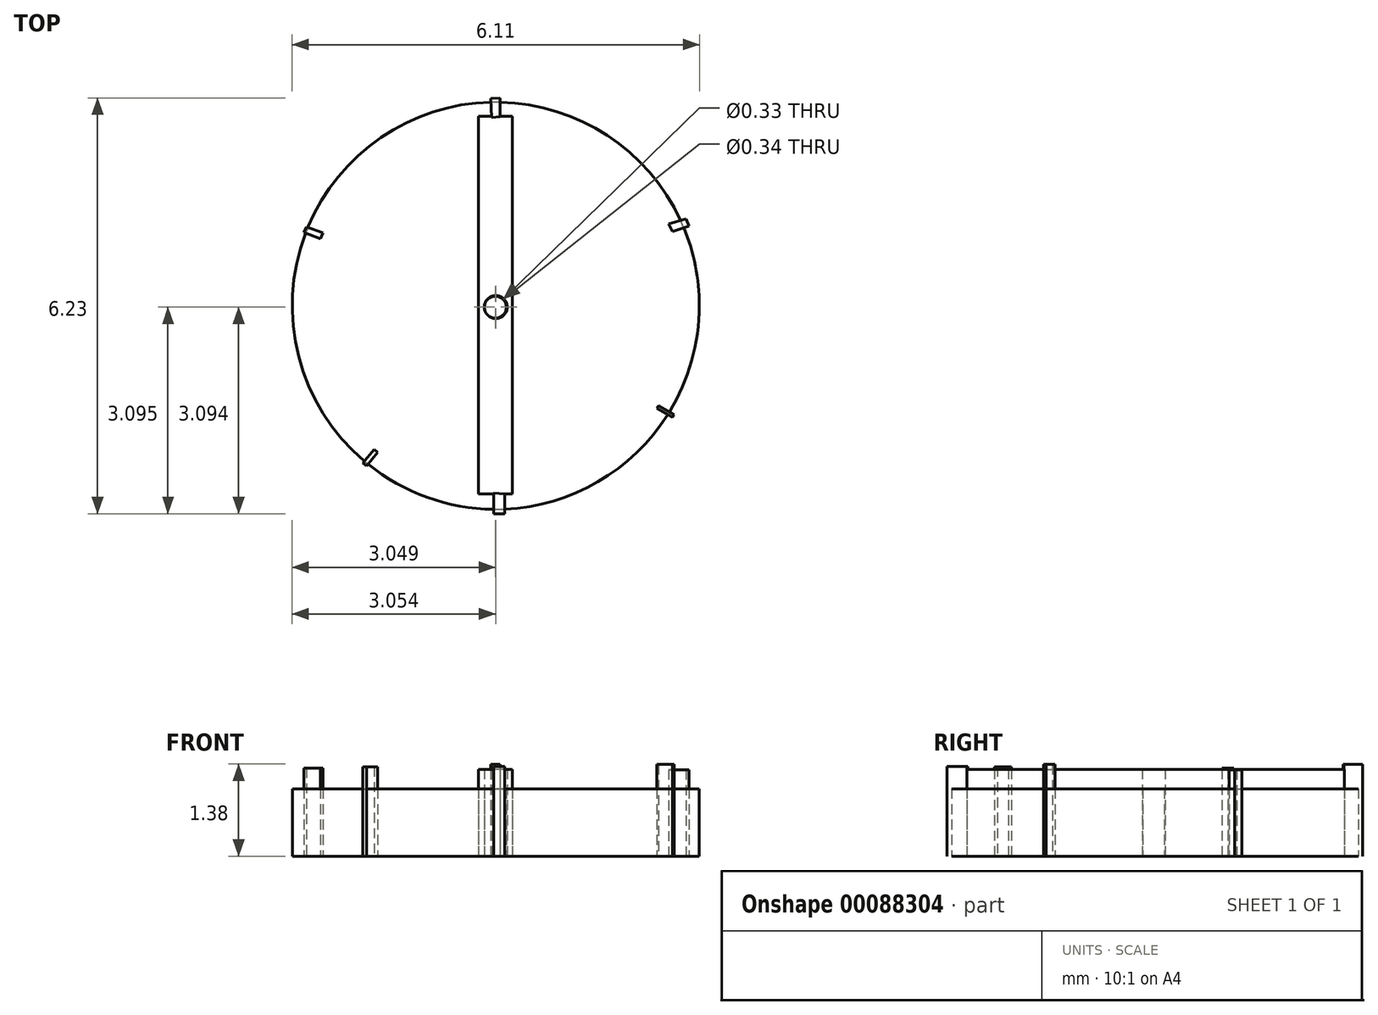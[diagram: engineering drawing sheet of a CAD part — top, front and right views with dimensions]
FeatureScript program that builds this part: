
annotation { "Feature Type Name" : "Feature", "Feature Type Description" : "" }
export const myFeature = defineFeature(function(context is Context, id is Id, definition is map)
    precondition{}
    {
        {
            var Q0;
            Q0=qCreatedBy(makeId("Top.planeOp"),FACE);
            var sketch = newSketch(context, id + "F0", { "sketchPlane" : qUnion([Q0])});
            skLineSegment(sketch, "E0", {"start": v(-40, 21.65) * mm, "end": v(-40, 15.99) * mm});
            skLineSegment(sketch, "E1", {"start": v(-40, 15.99) * mm, "end": v(-39.49, 15.99) * mm});
            skLineSegment(sketch, "E2", {"start": v(-39.49, 15.99) * mm, "end": v(-39.49, 21.65) * mm});
            skLineSegment(sketch, "E3", {"start": v(-39.49, 21.65) * mm, "end": v(-40, 21.65) * mm});
            skCircle(sketch, "E4", {"center": v(-39.77, 18.82) * mm, "radius": 2.9 * mm});
            skPoint(sketch, "E4.centerSnap0", {"position": v(-40, 18.82) * mm});
            skCircle(sketch, "E5", {"center": v(-39.77, 18.82) * mm, "radius": 3.38 * mm});
            skSolve(sketch);
        }
        {
            var Q0;
            Q0=makeQuery(id+"F0.imprint","IMPRINT",FACE,{"disambiguationData":[TD([[makeQuery(id+"F0.imprint","IMPRINT",EDGE,{"derivedFrom":sQuery(id+"F0.wireOp",EDGE,"E0")}),1.0]])]});
            extrude(context, id + "F1", {"entities" : qUnion([Q0]), "depth" : 1.3 * mm});
        }
        {
            var Q0;
            Q0=qCreatedBy(makeId("Top.planeOp"),FACE);
            var sketch = newSketch(context, id + "F2", { "sketchPlane" : qUnion([Q0])});
            skLineSegment(sketch, "E6", {"start": v(-42.36, 19.8) * mm, "end": v(-42.61, 19.9) * mm});
            skLineSegment(sketch, "E7", {"start": v(-42.33, 19.9) * mm, "end": v(-42.58, 19.99) * mm});
            skLineSegment(sketch, "E8", {"start": v(-42.33, 19.9) * mm, "end": v(-42.36, 19.8) * mm});
            skLineSegment(sketch, "E9", {"start": v(-42.58, 19.99) * mm, "end": v(-42.61, 19.9) * mm});
            skSolve(sketch);
        }
        {
            var Q0;
            Q0 = qSketchRegion(id + "F2", true);
            extrude(context, id + "F3", {"entities" : qUnion([Q0]), "depth" : 1.32 * mm});
        }
        {
            var Q0;
            Q0=qCreatedBy(makeId("Top.planeOp"),FACE);
            var sketch = newSketch(context, id + "F4", { "sketchPlane" : qUnion([Q0])});
            skLineSegment(sketch, "E10", {"start": v(-37.09, 19.92) * mm, "end": v(-36.84, 20) * mm});
            skLineSegment(sketch, "E11", {"start": v(-37.14, 20.03) * mm, "end": v(-36.88, 20.11) * mm});
            skLineSegment(sketch, "E12", {"start": v(-36.88, 20.11) * mm, "end": v(-36.84, 20) * mm});
            skLineSegment(sketch, "E13", {"start": v(-37.09, 19.92) * mm, "end": v(-37.14, 20.03) * mm});
            skSolve(sketch);
        }
        {
            var Q0;
            Q0 = qSketchRegion(id + "F4", true);
            extrude(context, id + "F5", {"entities" : qUnion([Q0]), "depth" : 1.3 * mm});
        }
        {
            var Q0;
            Q0=qCreatedBy(makeId("Top.planeOp"),FACE);
            var sketch = newSketch(context, id + "F6", { "sketchPlane" : qUnion([Q0])});
            skLineSegment(sketch, "E14", {"start": v(-41.67, 16.4) * mm, "end": v(-41.5, 16.61) * mm});
            skLineSegment(sketch, "E15", {"start": v(-41.73, 16.45) * mm, "end": v(-41.56, 16.65) * mm});
            skLineSegment(sketch, "E16", {"start": v(-41.56, 16.65) * mm, "end": v(-41.5, 16.61) * mm});
            skLineSegment(sketch, "E17", {"start": v(-41.67, 16.4) * mm, "end": v(-41.73, 16.45) * mm});
            skSolve(sketch);
        }
        {
            var Q0;
            Q0 = qSketchRegion(id + "F6", true);
            extrude(context, id + "F7", {"entities" : qUnion([Q0]), "depth" : 1.34 * mm});
        }
        {
            var Q0;
            Q0=qCreatedBy(makeId("Top.planeOp"),FACE);
            var sketch = newSketch(context, id + "F8", { "sketchPlane" : qUnion([Q0])});
            skLineSegment(sketch, "E18", {"start": v(-37.3, 17.3) * mm, "end": v(-37.06, 17.17) * mm});
            skLineSegment(sketch, "E19", {"start": v(-37.06, 17.17) * mm, "end": v(-37.08, 17.14) * mm});
            skLineSegment(sketch, "E20", {"start": v(-37.08, 17.14) * mm, "end": v(-37.32, 17.27) * mm});
            skLineSegment(sketch, "E21", {"start": v(-37.32, 17.27) * mm, "end": v(-37.3, 17.3) * mm});
            skSolve(sketch);
        }
        {
            var Q0;
            Q0 = qSketchRegion(id + "F8", true);
            extrude(context, id + "F9", {"entities" : qUnion([Q0]), "depth" : 1.37 * mm});
        }
        {
            var Q0;
            Q0=qCreatedBy(makeId("Top.planeOp"),FACE);
            var sketch = newSketch(context, id + "F10", { "sketchPlane" : qUnion([Q0])});
            skLineSegment(sketch, "E22", {"start": v(-39.6, 15.99) * mm, "end": v(-39.6, 15.69) * mm});
            skLineSegment(sketch, "E23", {"start": v(-39.6, 15.69) * mm, "end": v(-39.77, 15.69) * mm});
            skLineSegment(sketch, "E24", {"start": v(-39.77, 15.69) * mm, "end": v(-39.77, 16) * mm});
            skLineSegment(sketch, "E25", {"start": v(-39.77, 16) * mm, "end": v(-39.6, 15.99) * mm});
            skSolve(sketch);
        }
        {
            var Q0;
            Q0 = qSketchRegion(id + "F10", true);
            extrude(context, id + "F11", {"entities" : qUnion([Q0]), "operationType" : NewBodyOperationType.ADD, "depth" : 1.35 * mm});
        }
        {
            var Q0;
            Q0=qCreatedBy(makeId("Top.planeOp"),FACE);
            var sketch = newSketch(context, id + "F12", { "sketchPlane" : qUnion([Q0])});
            skLineSegment(sketch, "E26", {"start": v(-39.67, 21.64) * mm, "end": v(-39.67, 21.92) * mm});
            skLineSegment(sketch, "E27", {"start": v(-39.67, 21.92) * mm, "end": v(-39.8, 21.91) * mm});
            skLineSegment(sketch, "E28", {"start": v(-39.8, 21.91) * mm, "end": v(-39.8, 21.63) * mm});
            skLineSegment(sketch, "E29", {"start": v(-39.8, 21.63) * mm, "end": v(-39.67, 21.64) * mm});
            skSolve(sketch);
        }
        {
            var Q0;
            Q0 = qSketchRegion(id + "F12", true);
            extrude(context, id + "F13", {"entities" : qUnion([Q0]), "operationType" : NewBodyOperationType.ADD, "depth" : 1.38 * mm});
        }
        {
            var Q0;
            Q0=qCreatedBy(makeId("Top.planeOp"),FACE);
            var sketch = newSketch(context, id + "F14", { "sketchPlane" : qUnion([Q0])});
            skCircle(sketch, "E30", {"center": v(-39.74, 18.79) * mm, "radius": 0.17 * mm});
            skSolve(sketch);
        }
        {
            var Q0;
            Q0 = qSketchRegion(id + "F14", true);
            extrude(context, id + "F15", {"entities" : qUnion([Q0]), "operationType" : NewBodyOperationType.REMOVE, "depth" : 25.4 * mm});
        }
        {
            var Q0;
            Q0=qCreatedBy(makeId("Top.planeOp"),FACE);
            var sketch = newSketch(context, id + "F16", { "sketchPlane" : qUnion([Q0])});
            skCircle(sketch, "E31", {"center": v(-39.73, 18.8) * mm, "radius": 3.05 * mm});
            skSolve(sketch);
        }
        {
            var Q0;
            Q0 = qSketchRegion(id + "F16", true);
            extrude(context, id + "F17", {"entities" : qUnion([Q0]), "depth" : 1 * mm});
        }
        {
            var Q0;
            Q0=qCreatedBy(makeId("Top.planeOp"),FACE);
            var sketch = newSketch(context, id + "F18", { "sketchPlane" : qUnion([Q0])});
            skCircle(sketch, "E32", {"center": v(-39.74, 18.78) * mm, "radius": 0.16 * mm});
            skSolve(sketch);
        }
        {
            var Q0;
            Q0 = qSketchRegion(id + "F18", true);
            extrude(context, id + "F19", {"entities" : qUnion([Q0]), "operationType" : NewBodyOperationType.REMOVE, "depth" : 25.4 * mm});
        }
    });
